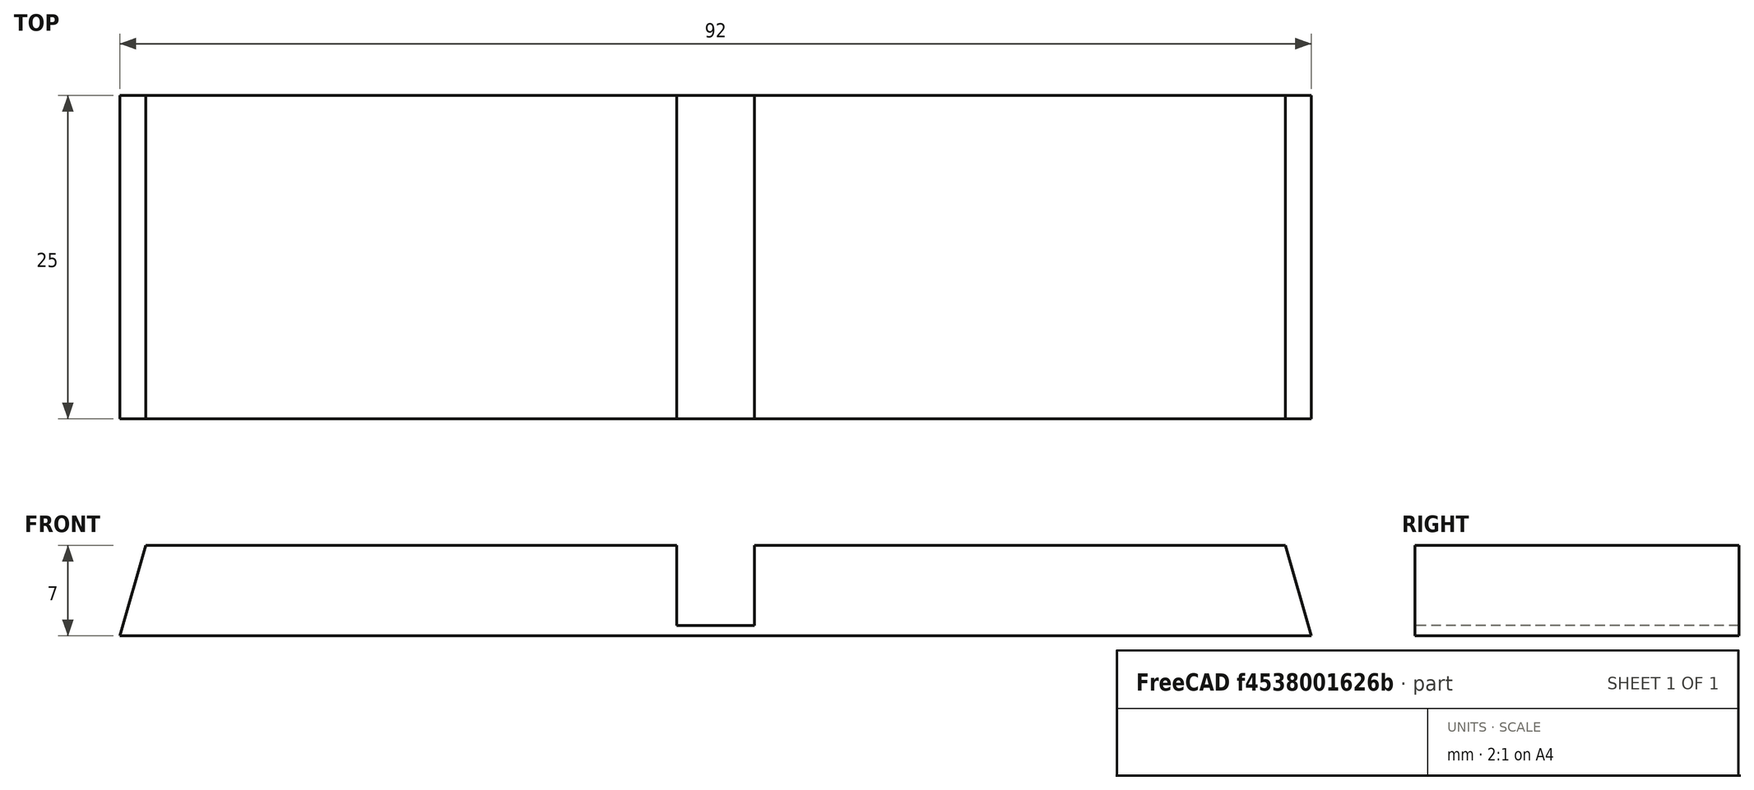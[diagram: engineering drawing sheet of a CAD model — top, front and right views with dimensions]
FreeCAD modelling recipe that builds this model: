
FCSTD DOCUMENT  (FreeCAD 0.20R28647 (Git))
Label: ello-cane-adapter
License: All rights reserved
LicenseURL: http://en.wikipedia.org/wiki/All_rights_reserved
objects: Sketcher::SketchObject×1, PartDesign::Pad×1, PartDesign::Body×1
note: 4 computed .brp shape members not serialized (recipe doc carries the construction recipe); baked Part::Feature solids carry a one-line shape summary decoded from their .brp

FEATURE [Sketcher::SketchObject] Sketch
  FullyConstrained = true
  MapMode = 5
  Placement = pos=(0,0,0) rot=(1,0,0;1.5708rad)
  Support = -> [XZ_Plane]
  sketch-geometry (8):
    g0: LineSegment StartX=-46 StartY=0 StartZ=0 EndX=46 EndY=0 EndZ=0
    g1: LineSegment StartX=46 StartY=0 StartZ=0 EndX=44 EndY=7 EndZ=0
    g2: LineSegment StartX=44 StartY=7 StartZ=0 EndX=3 EndY=7 EndZ=0
    g3: LineSegment StartX=-44 StartY=7 StartZ=0 EndX=-46 EndY=0 EndZ=0
    g4: LineSegment StartX=-3 StartY=7 StartZ=0 EndX=-3 EndY=0.8 EndZ=0
    g5: LineSegment StartX=-3 StartY=0.8 StartZ=0 EndX=3 EndY=0.8 EndZ=0
    g6: LineSegment StartX=3 StartY=0.8 StartZ=0 EndX=3 EndY=7 EndZ=0
    g7: LineSegment StartX=-3 StartY=7 StartZ=0 EndX=-44 EndY=7 EndZ=0
  constraints (22):
    c: Coincident(g0,g1)
    c: Coincident(g1,g2)
    c: Coincident(g7,g3)
    c: Coincident(g3,g0)
    c: Horizontal(g2)
    c: PointOnObject(g0,g-1)
    c: Vertical(g4)
    c: Coincident(g4,g5)
    c: Horizontal(g5)
    c: Coincident(g5,g6)
    c: Vertical(g6)
    c: Coincident(g2,g6)
    c: Coincident(g7,g4)
    c: Symmetric(g0,g0,g-2)
    c: Symmetric(g4,g2,g-2)
    c: Horizontal(g7)
    c: DistanceY(g4) = 0.8
    c: DistanceY(g1,g1) = 7
    c: DistanceX(g2,g2) = 41
    c: DistanceX(g5,g5) = 6
    c: DistanceX(g1,g0) = 2
    c: Equal(g2,g7)
FEATURE [PartDesign::Pad] Pad
  Direction = (0,-1,2e-16)
  Length = 25
  Length2 = 10
  Placement = pos=(0,0,0) rot=(1,0,0;1.5708rad)
  Profile = -> Sketch
  ReferenceAxis = -> Sketch [N_Axis]
  Type = 0
FEATURE [PartDesign::Body] Body
  Group = -> [Sketch,Pad]
  Origin = -> Origin
  Tip = -> Pad
